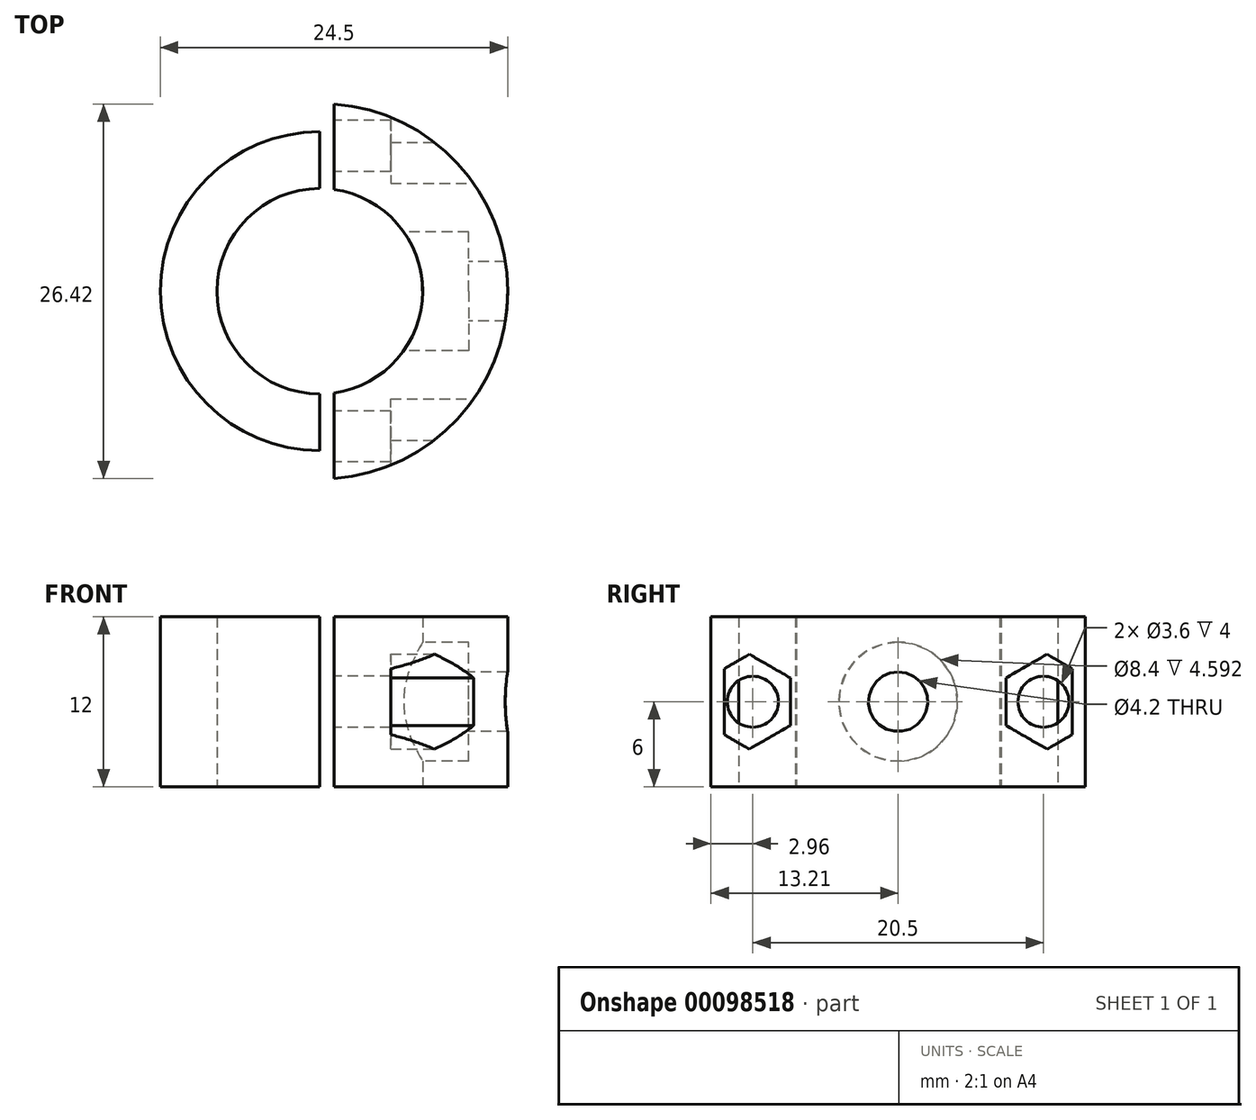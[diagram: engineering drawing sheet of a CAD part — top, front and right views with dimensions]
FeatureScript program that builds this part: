
annotation { "Feature Type Name" : "Feature", "Feature Type Description" : "" }
export const myFeature = defineFeature(function(context is Context, id is Id, definition is map)
    precondition{}
    {
        {
            var Q0;
            Q0=qCreatedBy(makeId("Top.planeOp"),FACE);
            var sketch = newSketch(context, id + "F0", { "sketchPlane" : qUnion([Q0])});
            skCircle(sketch, "E0", {"center": v(0, 0) * mm, "radius": 7.25 * mm});
            skCircle(sketch, "E1", {"center": v(0, 0) * mm, "radius": 11.25 * mm});
            skCircle(sketch, "E2", {"center": v(0, 0) * mm, "radius": 13.25 * mm});
            skLineSegment(sketch, "E3", {"start": v(0, 0) * mm, "end": v(0, 13.25) * mm});
            skLineSegment(sketch, "E4", {"start": v(0, 13.25) * mm, "end": v(0, -13.25) * mm});
            skLineSegment(sketch, "E5", {"start": v(0, 0) * mm, "end": v(0, 4) * mm});
            skLineSegment(sketch, "E6", {"start": v(0, 0) * mm, "end": v(0, -4) * mm});
            skLineSegment(sketch, "E7", {"start": v(0, 4) * mm, "end": v(10.51, 4) * mm});
            skLineSegment(sketch, "E8", {"start": v(0, -4) * mm, "end": v(10.51, -4) * mm});
            skLineSegment(sketch, "E9", {"start": v(11.25, 0) * mm, "end": v(0, 0) * mm});
            skLineSegment(sketch, "E10.top", {"start": v(11.25, 4) * mm, "end": v(0, 4) * mm});
            skLineSegment(sketch, "E10.left", {"start": v(11.25, 0) * mm, "end": v(11.25, 4) * mm});
            skLineSegment(sketch, "E11.top", {"start": v(11.25, -4) * mm, "end": v(0, -4) * mm});
            skLineSegment(sketch, "E11.left", {"start": v(11.25, 0) * mm, "end": v(11.25, -4) * mm});
            skSolve(sketch);
        }
        {
            var Q0;
            {var subQ9=sQuery(id+"F0.wireOp",EDGE,"E10.left");Q0=makeQuery(id+"F0.imprint","IMPRINT",FACE,{"disambiguationData":[TD([[makeQuery(id+"F0.imprint","IMPRINT",EDGE,{"derivedFrom":subQ9}),-1.0]])]});}
            var Q1;
            {var subQ0=sQuery(id+"F0.wireOp",EDGE,"E4");var subQ1=sQuery(id+"F0.wireOp",EDGE,"E0");var subQ2=makeQuery(id+"F0.imprint","INTERSECT",VERTEX,{"disambiguationData":[OD(1.0)],"derivedFrom":[subQ1,subQ0]});Q1=makeQuery(id+"F0.imprint","IMPRINT",FACE,{"disambiguationData":[TD([[makeQuery(id+"F0.imprint","IMPRINT",EDGE,{"disambiguationData":[TD([[subQ2,-1.0]])],"derivedFrom":subQ1}),-1.0]])]});}
            var Q2;
            {var subQ0=sQuery(id+"F0.wireOp",EDGE,"E9");var subQ1=sQuery(id+"F0.wireOp",EDGE,"E0");var subQ2=makeQuery(id+"F0.imprint","INTERSECT",VERTEX,{"derivedFrom":[subQ1,subQ0]});Q2=makeQuery(id+"F0.imprint","IMPRINT",FACE,{"disambiguationData":[TD([[makeQuery(id+"F0.imprint","IMPRINT",EDGE,{"disambiguationData":[TD([[subQ2,1.0]])],"derivedFrom":subQ1}),-1.0]])]});}
            var Q3;
            {var subQ0=sQuery(id+"F0.wireOp",EDGE,"E10.top");var subQ1=sQuery(id+"F0.wireOp",EDGE,"E0");var subQ2=makeQuery(id+"F0.imprint","INTERSECT",VERTEX,{"derivedFrom":[subQ1,subQ0]});Q3=makeQuery(id+"F0.imprint","IMPRINT",FACE,{"disambiguationData":[TD([[makeQuery(id+"F0.imprint","IMPRINT",EDGE,{"disambiguationData":[TD([[subQ2,1.0]])],"derivedFrom":subQ1}),-1.0]])]});}
            var Q4;
            {var subQ0=sQuery(id+"F0.wireOp",EDGE,"E10.left");Q4=makeQuery(id+"F0.imprint","IMPRINT",FACE,{"disambiguationData":[TD([[makeQuery(id+"F0.imprint","IMPRINT",EDGE,{"derivedFrom":subQ0}),1.0]])]});}
            var Q5;
            {var subQ0=sQuery(id+"F0.wireOp",EDGE,"E11.left");Q5=makeQuery(id+"F0.imprint","IMPRINT",FACE,{"disambiguationData":[TD([[makeQuery(id+"F0.imprint","IMPRINT",EDGE,{"derivedFrom":subQ0}),-1.0]])]});}
            var Q6;
            {var subQ0=sQuery(id+"F0.wireOp",EDGE,"E10.top");var subQ1=sQuery(id+"F0.wireOp",EDGE,"E0");var subQ2=makeQuery(id+"F0.imprint","INTERSECT",VERTEX,{"derivedFrom":[subQ1,subQ0]});Q6=makeQuery(id+"F0.imprint","IMPRINT",FACE,{"disambiguationData":[TD([[makeQuery(id+"F0.imprint","IMPRINT",EDGE,{"disambiguationData":[TD([[subQ2,-1.0]])],"derivedFrom":subQ1}),-1.0]])]});}
            extrude(context, id + "F1", {"entities" : qUnion([Q0, Q1, Q2, Q3, Q4, Q5, Q6]), "depth" : 12 * mm});
        }
        {
            var Q0;
            Q0=qCreatedBy(makeId("Right.planeOp"),FACE);
            var sketch = newSketch(context, id + "F2", { "sketchPlane" : qUnion([Q0])});
            skLineSegment(sketch, "E12", {"start": v(0, 0) * mm, "end": v(0, 6) * mm});
            skCircle(sketch, "E13", {"center": v(0, 6) * mm, "radius": 4.2 * mm});
            skCircle(sketch, "E14", {"center": v(0, 6) * mm, "radius": 2.1 * mm});
            skSolve(sketch);
        }
        {
            var Q0;
            Q0 = qSketchRegion(id + "F2", true);
            var Q1;
            Q1=makeQuery(id+"F2.imprint","IMPRINT",FACE,{"disambiguationData":[TD([[makeQuery(id+"F2.imprint","IMPRINT",EDGE,{"derivedFrom":sQuery(id+"F2.wireOp",EDGE,"E14")}),1.0]])]});
            extrude(context, id + "F3", {"entities" : qUnion([Q0, Q1]), "operationType" : NewBodyOperationType.REMOVE, "depth" : 10.5 * mm});
        }
        {
            var Q0;
            Q0=makeQuery(id+"F2.imprint","IMPRINT",FACE,{"disambiguationData":[TD([[makeQuery(id+"F2.imprint","IMPRINT",EDGE,{"derivedFrom":sQuery(id+"F2.wireOp",EDGE,"E14")}),1.0]])]});
            extrude(context, id + "F4", {"entities" : qUnion([Q0]), "operationType" : NewBodyOperationType.REMOVE, "depth" : 25 * mm});
        }
        {
            var Q0;
            Q0=makeQuery(id+"F1.opExtrude","CAP_FACE",FACE,{"disambiguationData":[OSD([sQuery(id+"F0.wireOp",EDGE,"E0"),sQuery(id+"F0.wireOp",EDGE,"E2"),sQuery(id+"F0.wireOp",EDGE,"E4")])],"isStart":false});
            var sketch = newSketch(context, id + "F5", { "sketchPlane" : qUnion([Q0])});
            skLineSegment(sketch, "E15", {"start": v(0, 0) * mm, "end": v(11.47, 6.62) * mm});
            skLineSegment(sketch, "E16", {"start": v(0, 0) * mm, "end": v(11.47, -6.62) * mm});
            skCircle(sketch, "E17", {"center": v(0, 0) * mm, "radius": 10.5 * mm});
            skLineSegment(sketch, "E18", {"start": v(11.47, 6.62) * mm, "end": v(8.15, 6.62) * mm});
            skLineSegment(sketch, "E19", {"start": v(11.47, -6.62) * mm, "end": v(8.15, -6.62) * mm});
            skSolve(sketch);
        }
        {
            var Q0;
            {var subQ0=sQuery(id+"F0.wireOp",EDGE,"E4");Q0=makeQuery(id+"F1.opExtrude","SWEPT_FACE",FACE,{"disambiguationData":[OSD([subQ0]),TDD([makeQuery(id+"F0.imprint","IMPRINT",EDGE,{"disambiguationData":[TD([[makeQuery(id+"F0.imprint","INTERSECT",VERTEX,{"disambiguationData":[OD(1.0)],"derivedFrom":[sQuery(id+"F0.wireOp",EDGE,"E0"),subQ0]}),-1.0]])],"derivedFrom":subQ0}),makeQuery(id+"F0.imprint","IMPRINT",EDGE,{"disambiguationData":[TD([[makeQuery(id+"F0.imprint","INTERSECT",VERTEX,{"disambiguationData":[OD(1.0)],"derivedFrom":[sQuery(id+"F0.wireOp",EDGE,"E2"),subQ0]}),1.0]])],"derivedFrom":subQ0})])]});}
            var sketch = newSketch(context, id + "F6", { "sketchPlane" : qUnion([Q0])});
            skLineSegment(sketch, "E20", {"start": v(7.25, 6) * mm, "end": v(13.25, 6) * mm});
            skCircle(sketch, "E21", {"center": v(10.25, 6) * mm, "radius": 1.8 * mm});
            skSolve(sketch);
        }
        {
            var Q0;
            Q0 = qSketchRegion(id + "F6", true);
            extrude(context, id + "F7", {"entities" : qUnion([Q0]), "operationType" : NewBodyOperationType.REMOVE, "oppositeDirection" : true, "depth" : 25 * mm});
        }
        {
            var Q0;
            {var subQ0=sQuery(id+"F0.wireOp",EDGE,"E4");Q0=makeQuery(id+"F1.opExtrude","SWEPT_FACE",FACE,{"disambiguationData":[OSD([subQ0]),TDD([makeQuery(id+"F0.imprint","IMPRINT",EDGE,{"disambiguationData":[TD([[makeQuery(id+"F0.imprint","INTERSECT",VERTEX,{"disambiguationData":[OD(0.0)],"derivedFrom":[sQuery(id+"F0.wireOp",EDGE,"E2"),subQ0]}),-1.0]])],"derivedFrom":subQ0}),makeQuery(id+"F0.imprint","IMPRINT",EDGE,{"disambiguationData":[TD([[makeQuery(id+"F0.imprint","INTERSECT",VERTEX,{"disambiguationData":[OD(0.0)],"derivedFrom":[sQuery(id+"F0.wireOp",EDGE,"E0"),subQ0]}),1.0]])],"derivedFrom":subQ0})])]});}
            var sketch = newSketch(context, id + "F8", { "sketchPlane" : qUnion([Q0])});
            skLineSegment(sketch, "E22", {"start": v(-7.25, 6) * mm, "end": v(-13.25, 6) * mm});
            skCircle(sketch, "E23", {"center": v(-10.25, 6) * mm, "radius": 1.8 * mm});
            skSolve(sketch);
        }
        {
            var Q0;
            {var subQ0=sQuery(id+"F8.wireOp",EDGE,"E23");var subQ1=sQuery(id+"F8.wireOp",EDGE,"E22");var subQ2=makeQuery(id+"F8.imprint","INTERSECT",VERTEX,{"disambiguationData":[OD(0.0)],"derivedFrom":[subQ1,subQ0]});Q0=makeQuery(id+"F8.imprint","IMPRINT",FACE,{"disambiguationData":[TD([[makeQuery(id+"F8.imprint","IMPRINT",EDGE,{"disambiguationData":[TD([[subQ2,-1.0]])],"derivedFrom":subQ1}),-1.0]])]});}
            var Q1;
            {var subQ0=sQuery(id+"F8.wireOp",EDGE,"E23");var subQ1=sQuery(id+"F8.wireOp",EDGE,"E22");var subQ2=makeQuery(id+"F8.imprint","INTERSECT",VERTEX,{"disambiguationData":[OD(0.0)],"derivedFrom":[subQ1,subQ0]});Q1=makeQuery(id+"F8.imprint","IMPRINT",FACE,{"disambiguationData":[TD([[makeQuery(id+"F8.imprint","IMPRINT",EDGE,{"disambiguationData":[TD([[subQ2,-1.0]])],"derivedFrom":subQ1}),1.0]])]});}
            extrude(context, id + "F9", {"entities" : qUnion([Q0, Q1]), "operationType" : NewBodyOperationType.REMOVE, "oppositeDirection" : true, "depth" : 25 * mm});
        }
        {
            var Q0;
            Q0=qCreatedBy(makeId("Right.planeOp"),FACE);
            cPlane(context, id + "F10", {"entities" : qUnion([Q0]), "cplaneType" : CPlaneType.OFFSET, "offset" : 13 * mm, "width" : 150 * mm, "height" : 150 * mm});
        }
        {
            var Q0;
            Q0=qCreatedBy(id+"F10.planeOp",FACE);
            var sketch = newSketch(context, id + "F11", { "sketchPlane" : qUnion([Q0])});
            skLineSegment(sketch, "E24", {"start": v(0, 0) * mm, "end": v(0, 6) * mm});
            skLineSegment(sketch, "E25", {"start": v(0, 6) * mm, "end": v(-10.5, 6) * mm});
            skLineSegment(sketch, "E26", {"start": v(0, 6) * mm, "end": v(10.5, 6) * mm});
            skCircle(sketch, "E27.cCircle", {"center": v(10.5, 6) * mm, "radius": 2.9 * mm, "construction": true});
            skLineSegment(sketch, "E27.0", {"start": v(7.6, 4.33) * mm, "end": v(7.6, 7.67) * mm});
            skLineSegment(sketch, "E27.1", {"start": v(7.6, 7.67) * mm, "end": v(10.5, 9.35) * mm});
            skLineSegment(sketch, "E27.2", {"start": v(10.5, 9.35) * mm, "end": v(13.4, 7.67) * mm});
            skLineSegment(sketch, "E27.3", {"start": v(13.4, 7.67) * mm, "end": v(13.4, 4.33) * mm});
            skLineSegment(sketch, "E27.4", {"start": v(13.4, 4.33) * mm, "end": v(10.5, 2.65) * mm});
            skLineSegment(sketch, "E27.5", {"start": v(10.5, 2.65) * mm, "end": v(7.6, 4.33) * mm});
            skPoint(sketch, "E27.0.midPoint", {"position": v(7.6, 6) * mm});
            skCircle(sketch, "E28.cCircle", {"center": v(-10.5, 6) * mm, "radius": 2.9 * mm, "construction": true});
            skLineSegment(sketch, "E28.0", {"start": v(-7.6, 7.67) * mm, "end": v(-7.6, 4.33) * mm});
            skLineSegment(sketch, "E28.1", {"start": v(-7.6, 4.33) * mm, "end": v(-10.5, 2.65) * mm});
            skLineSegment(sketch, "E28.2", {"start": v(-10.5, 2.65) * mm, "end": v(-13.4, 4.33) * mm});
            skLineSegment(sketch, "E28.3", {"start": v(-13.4, 4.33) * mm, "end": v(-13.4, 7.67) * mm});
            skLineSegment(sketch, "E28.4", {"start": v(-13.4, 7.67) * mm, "end": v(-10.5, 9.35) * mm});
            skLineSegment(sketch, "E28.5", {"start": v(-10.5, 9.35) * mm, "end": v(-7.6, 7.67) * mm});
            skPoint(sketch, "E28.0.midPoint", {"position": v(-7.6, 6) * mm});
            skSolve(sketch);
        }
        {
            var Q0;
            Q0 = qSketchRegion(id + "F11", true);
            extrude(context, id + "F12", {"entities" : qUnion([Q0]), "operationType" : NewBodyOperationType.REMOVE, "oppositeDirection" : true, "depth" : 8 * mm});
        }
        {
            var Q0;
            Q0=qCreatedBy(makeId("Top.planeOp"),FACE);
            var sketch = newSketch(context, id + "F13", { "sketchPlane" : qUnion([Q0])});
            skLineSegment(sketch, "E29.bottom", {"start": v(0, 0) * mm, "end": v(1, 0) * mm});
            skLineSegment(sketch, "E29.top", {"start": v(0, 20) * mm, "end": v(1, 20) * mm});
            skLineSegment(sketch, "E29.left", {"start": v(0, 0) * mm, "end": v(0, 20) * mm});
            skLineSegment(sketch, "E29.right", {"start": v(1, 0) * mm, "end": v(1, 20) * mm});
            skLineSegment(sketch, "E30.top", {"start": v(0, -18.98) * mm, "end": v(1, -18.98) * mm});
            skLineSegment(sketch, "E30.left", {"start": v(0, 0) * mm, "end": v(0, -18.98) * mm});
            skLineSegment(sketch, "E30.right", {"start": v(1, 0) * mm, "end": v(1, -18.98) * mm});
            skSolve(sketch);
        }
        {
            var Q0;
            Q0 = qSketchRegion(id + "F13", true);
            extrude(context, id + "F14", {"entities" : qUnion([Q0]), "operationType" : NewBodyOperationType.REMOVE, "endBound" : BoundingType.SYMMETRIC, "oppositeDirection" : true, "depth" : 25 * mm});
        }
    });
